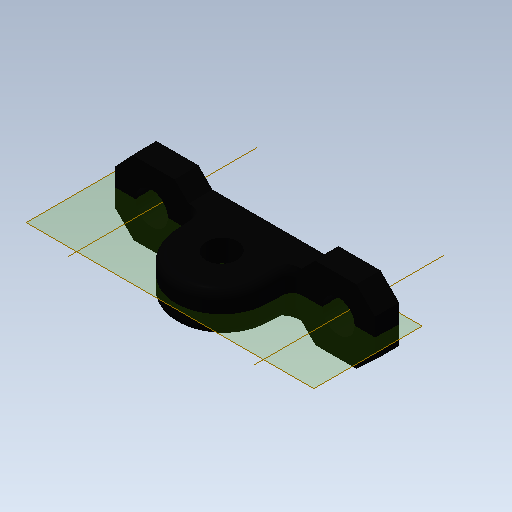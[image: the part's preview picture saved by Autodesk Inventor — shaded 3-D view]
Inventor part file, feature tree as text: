
AUTODESK INVENTOR PART (.ipt)
format: ipt  version: 2020 (Build 240168000, 168)  size: 378,368 bytes
history: native  units: in
note: dims shown in document units (in); Inventor stores cm internally (conversion verified against a paired STEP export)
features: other x4, plane x1, imported_body x1
ambient origin geometry x8: Origin, YZ Plane, XZ Plane, XY Plane, X Axis, Y Axis, Z Axis, Center Point
bodies: Body1 (feature_tree)
feature tree (6):
  other  "Pillow Block"
  parser-record x1  (decoder bookkeeping rows leaked as tree rows — omitted from the tree; the rows remain in map.json)
  plane  "Work Plane1"
  imported_body  "Base1"
  other  "Work Axis4"
  other  "Work Axis5"
